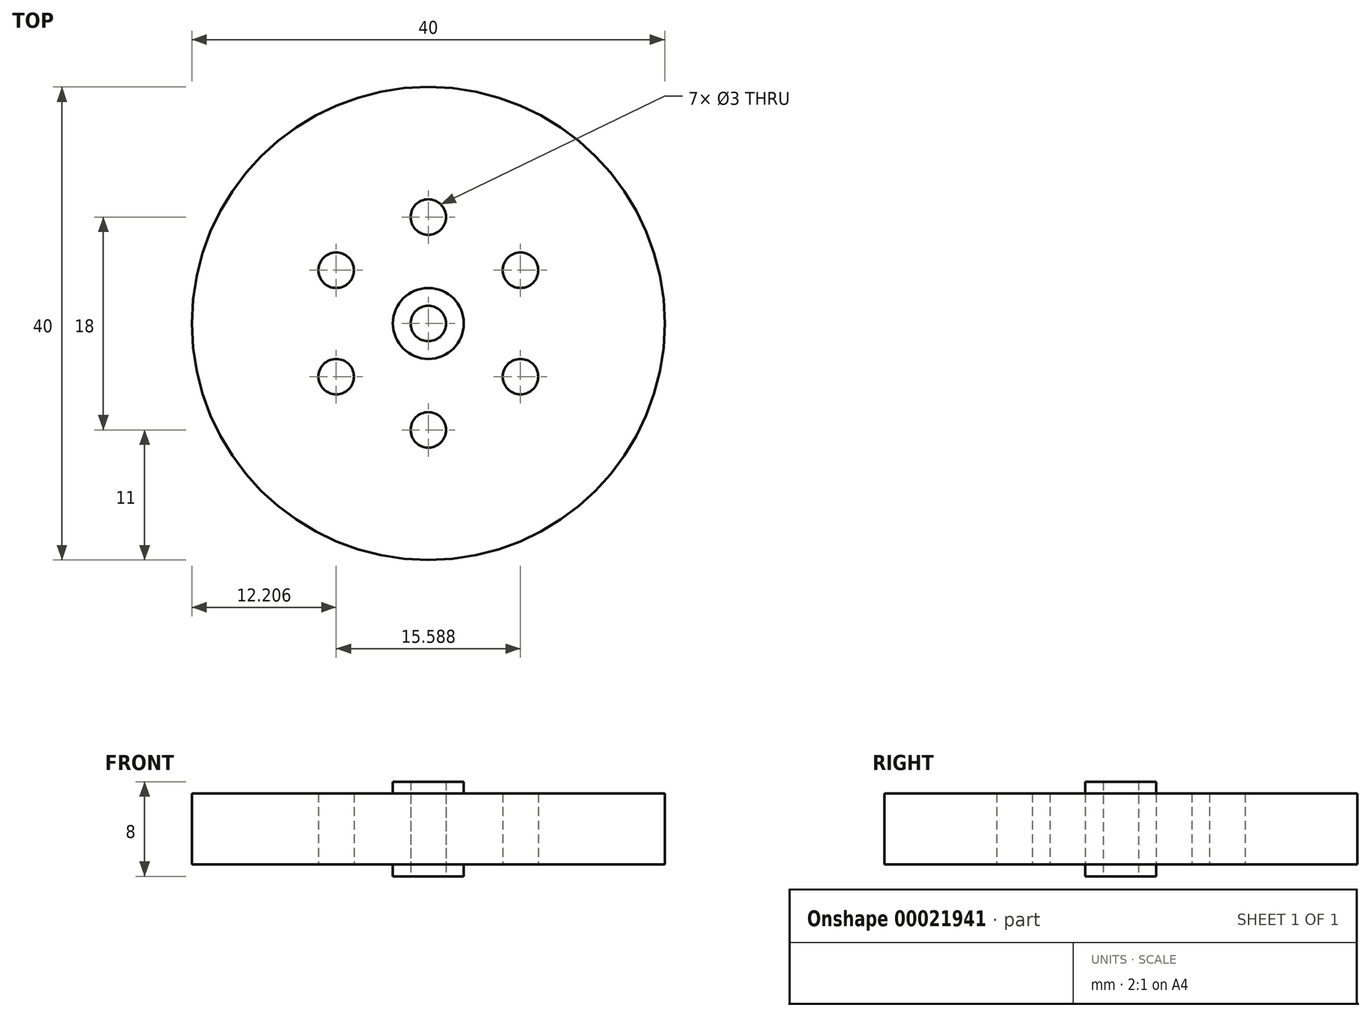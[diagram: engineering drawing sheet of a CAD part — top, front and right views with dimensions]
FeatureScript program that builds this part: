
annotation { "Feature Type Name" : "Feature", "Feature Type Description" : "" }
export const myFeature = defineFeature(function(context is Context, id is Id, definition is map)
    precondition{}
    {
        {
            var Q0;
            Q0=qCreatedBy(makeId("Top.planeOp"),FACE);
            var sketch = newSketch(context, id + "F0", { "sketchPlane" : qUnion([Q0])});
            skCircle(sketch, "E0", {"center": v(0, 0) * mm, "radius": 20 * mm});
            skCircle(sketch, "E1", {"center": v(0, 9) * mm, "radius": 1.5 * mm});
            skCircle(sketch, "E2.1.0", {"center": v(-7.8, 4.5) * mm, "radius": 1.5 * mm});
            skCircle(sketch, "E2.2.0", {"center": v(-7.8, -4.5) * mm, "radius": 1.5 * mm});
            skCircle(sketch, "E2.3.0", {"center": v(0, -9) * mm, "radius": 1.5 * mm});
            skCircle(sketch, "E2.4.0", {"center": v(7.8, -4.5) * mm, "radius": 1.5 * mm});
            skCircle(sketch, "E2.5.0", {"center": v(7.8, 4.5) * mm, "radius": 1.5 * mm});
            skSolve(sketch);
        }
        {
            var Q0;
            Q0=makeQuery(id+"F0.imprint","IMPRINT",FACE,{"disambiguationData":[TD([[makeQuery(id+"F0.imprint","IMPRINT",EDGE,{"derivedFrom":sQuery(id+"F0.wireOp",EDGE,"E0")}),1.0]])]});
            extrude(context, id + "F1", {"entities" : qUnion([Q0]), "depth" : 6 * mm});
        }
        {
            var Q0;
            Q0=makeQuery(id+"F1.opExtrude","CAP_FACE",FACE,{"disambiguationData":[OSD([sQuery(id+"F0.wireOp",EDGE,"E0"),sQuery(id+"F0.wireOp",EDGE,"E1"),sQuery(id+"F0.wireOp",EDGE,"E2.1.0"),sQuery(id+"F0.wireOp",EDGE,"E2.2.0"),sQuery(id+"F0.wireOp",EDGE,"E2.3.0"),sQuery(id+"F0.wireOp",EDGE,"E2.4.0"),sQuery(id+"F0.wireOp",EDGE,"E2.5.0")])],"isStart":false});
            var sketch = newSketch(context, id + "F2", { "sketchPlane" : qUnion([Q0])});
            skCircle(sketch, "E3", {"center": v(0, 0) * mm, "radius": 3 * mm});
            skCircle(sketch, "E4", {"center": v(0, 0) * mm, "radius": 1.5 * mm});
            skSolve(sketch);
        }
        {
            var Q0;
            Q0=makeQuery(id+"F2.imprint","IMPRINT",FACE,{"disambiguationData":[TD([[makeQuery(id+"F2.imprint","IMPRINT",EDGE,{"derivedFrom":sQuery(id+"F2.wireOp",EDGE,"E3")}),1.0]])]});
            extrude(context, id + "F3", {"entities" : qUnion([Q0]), "operationType" : NewBodyOperationType.ADD, "depth" : 1 * mm});
        }
        {
            var Q0;
            Q0=makeQuery(id+"F3.boolean.opBoolean","SPLIT",FACE,{"disambiguationData":[TD([makeQuery(id+"F3.opExtrude","SWEPT_FACE",FACE,{"disambiguationData":[OSD([sQuery(id+"F2.wireOp",EDGE,"E4")])]})])],"derivedFrom":makeQuery(id+"F1.opExtrude","CAP_FACE",FACE,{"disambiguationData":[OSD([sQuery(id+"F0.wireOp",EDGE,"E0"),sQuery(id+"F0.wireOp",EDGE,"E1"),sQuery(id+"F0.wireOp",EDGE,"E2.1.0"),sQuery(id+"F0.wireOp",EDGE,"E2.2.0"),sQuery(id+"F0.wireOp",EDGE,"E2.3.0"),sQuery(id+"F0.wireOp",EDGE,"E2.4.0"),sQuery(id+"F0.wireOp",EDGE,"E2.5.0")])],"isStart":false})});
            extrude(context, id + "F4", {"entities" : qUnion([Q0]), "operationType" : NewBodyOperationType.REMOVE, "oppositeDirection" : true, "depth" : 8 * mm});
        }
        {
            var Q0;
            Q0=makeQuery(id+"F1.opExtrude","CAP_FACE",FACE,{"disambiguationData":[OSD([sQuery(id+"F0.wireOp",EDGE,"E0"),sQuery(id+"F0.wireOp",EDGE,"E1"),sQuery(id+"F0.wireOp",EDGE,"E2.1.0"),sQuery(id+"F0.wireOp",EDGE,"E2.2.0"),sQuery(id+"F0.wireOp",EDGE,"E2.3.0"),sQuery(id+"F0.wireOp",EDGE,"E2.4.0"),sQuery(id+"F0.wireOp",EDGE,"E2.5.0")])],"isStart":true});
            var sketch = newSketch(context, id + "F5", { "sketchPlane" : qUnion([Q0])});
            skCircle(sketch, "E5", {"center": v(0, 0) * mm, "radius": 3 * mm});
            skSolve(sketch);
        }
        {
            var Q0;
            Q0=makeQuery(id+"F5.imprint","IMPRINT",FACE,{"disambiguationData":[TD([[makeQuery(id+"F5.imprint","IMPRINT",EDGE,{"derivedFrom":sQuery(id+"F5.wireOp",EDGE,"E5")}),1.0]])]});
            extrude(context, id + "F6", {"entities" : qUnion([Q0]), "operationType" : NewBodyOperationType.ADD, "depth" : 1 * mm});
        }
    });
